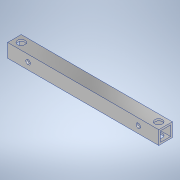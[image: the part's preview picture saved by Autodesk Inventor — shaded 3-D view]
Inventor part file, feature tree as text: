
AUTODESK INVENTOR PART (.ipt)
format: ipt  version: 2020.3 (Build 243373000, 373)  size: 141,824 bytes
history: native  units: mm
features: sketch x4, hole x3, other x1, extrude x1
ambient origin geometry x8: Origin, YZ Plane, XZ Plane, XY Plane, X Axis, Y Axis, Z Axis, Center Point
bodies: Body1 (feature_tree)
feature tree (9):
  other  "ソリッド1"
  extrude  "押し出し1"  Depth=9.0mm
  hole  "穴1"  [1 undecoded]
  hole  "穴2"  [1 undecoded]
  hole  "穴4"  [1 undecoded]
  sketch  "スケッチ1"
  sketch  "スケッチ2"
  sketch  "スケッチ3"
  sketch  "スケッチ5"
note: 3 required parameter values undecoded (feature->parameter linkage not recoverable at this tier; creation-order binding heuristic only, values carry confidence <= 0.55)
